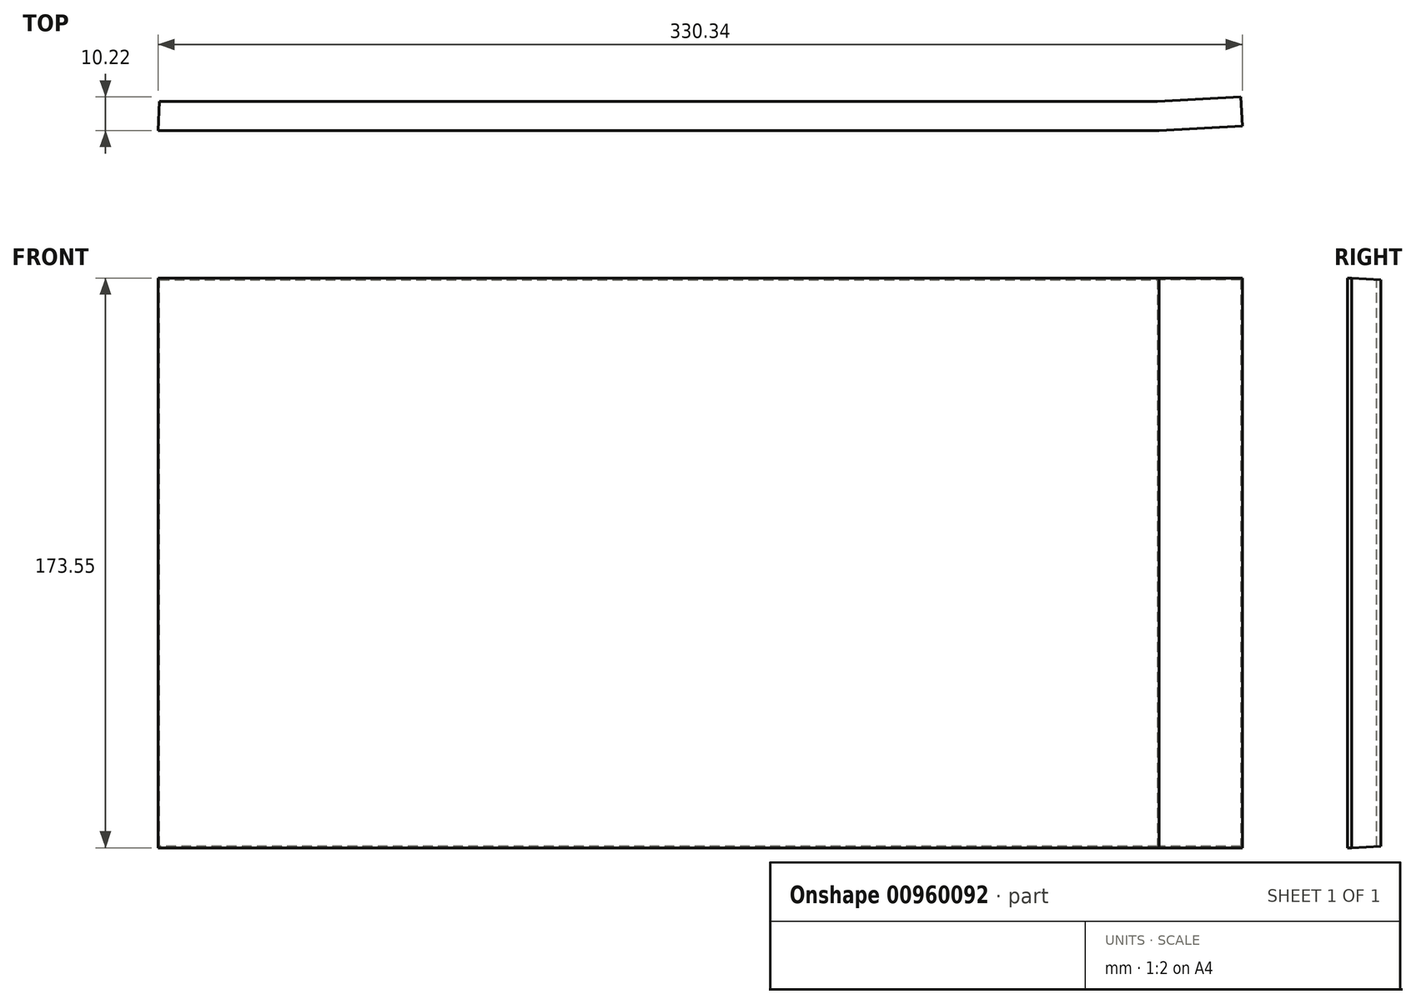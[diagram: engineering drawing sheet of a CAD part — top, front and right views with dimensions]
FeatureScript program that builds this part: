
annotation { "Feature Type Name" : "Feature", "Feature Type Description" : "" }
export const myFeature = defineFeature(function(context is Context, id is Id, definition is map)
    precondition{}
    {
        {
            var Q0;
            Q0=qCreatedBy(makeId("Front.planeOp"),FACE);
            var sketch = newSketch(context, id + "F0", { "sketchPlane" : qUnion([Q0])});
            skLineSegment(sketch, "E0.bottom", {"start": v(151.13, 85.6) * mm, "end": v(-152.92, 85.6) * mm});
            skLineSegment(sketch, "E0.top", {"start": v(151.13, -87.01) * mm, "end": v(-152.92, -87.01) * mm});
            skLineSegment(sketch, "E0.left", {"start": v(151.13, 85.6) * mm, "end": v(151.13, -87.01) * mm});
            skLineSegment(sketch, "E0.right", {"start": v(-152.92, 85.6) * mm, "end": v(-152.92, -87.01) * mm});
            skSolve(sketch);
        }
        {
            var Q0;
            Q0 = qSketchRegion(id + "F0", true);
            extrude(context, id + "F1", {"entities" : qUnion([Q0]), "depth" : 8.9 * mm, "offsetDistance" : 25.4 * mm, "hasDraft" : true, "draftAngle" : 3 * degree});
        }
        {
            var Q0;
            Q0=makeQuery(id+"F1.opExtrude","SWEPT_FACE",FACE,{"disambiguationData":[OSD([sQuery(id+"F0.wireOp",EDGE,"E0.left")])]});
            extrude(context, id + "F2", {"entities" : qUnion([Q0]), "operationType" : NewBodyOperationType.ADD, "depth" : 25.4 * mm, "offsetDistance" : 25.4 * mm});
        }
    });
